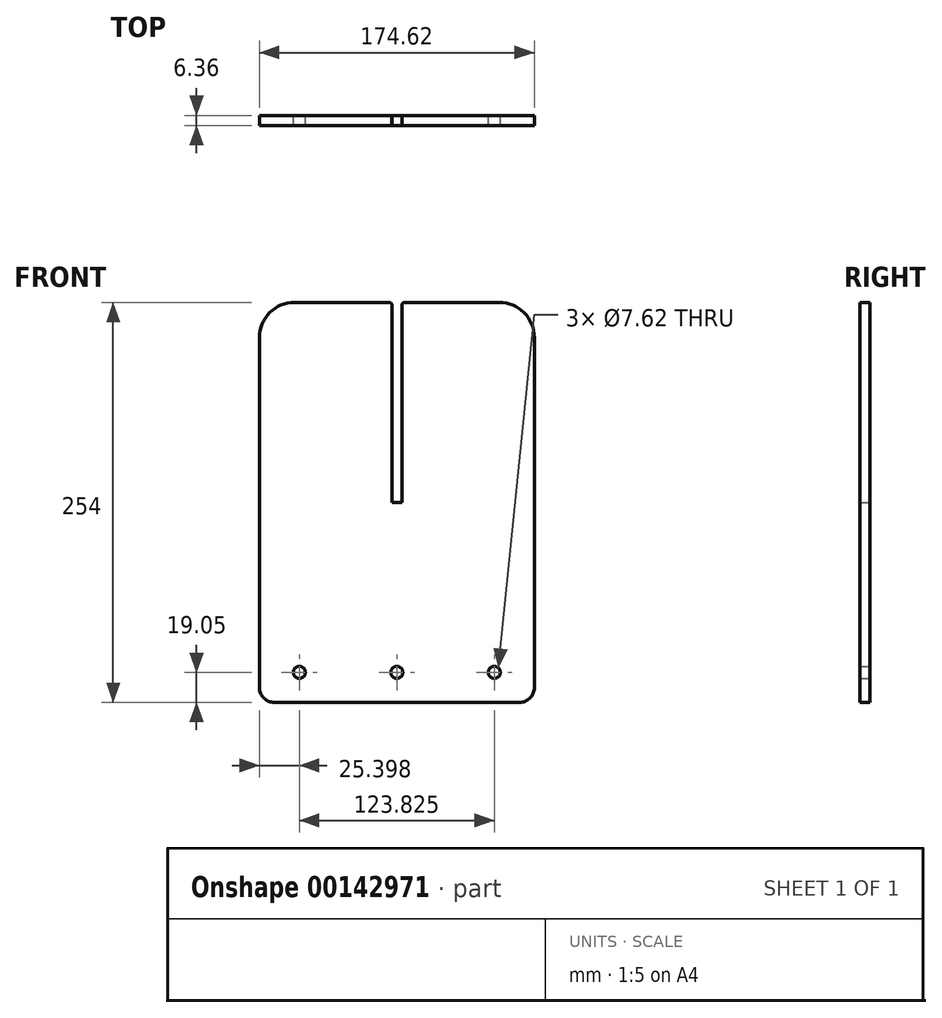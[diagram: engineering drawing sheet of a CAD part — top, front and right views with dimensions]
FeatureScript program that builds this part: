
annotation { "Feature Type Name" : "Feature", "Feature Type Description" : "" }
export const myFeature = defineFeature(function(context is Context, id is Id, definition is map)
    precondition{}
    {
        {
            var Q0;
            Q0=qCreatedBy(makeId("Front.planeOp"),FACE);
            var sketch = newSketch(context, id + "F0", { "sketchPlane" : qUnion([Q0])});
            skLineSegment(sketch, "E0.bottom", {"start": v(-65.09, 127) * mm, "end": v(-4.76, 127) * mm});
            skLineSegment(sketch, "E0.top", {"start": v(-77.79, -127) * mm, "end": v(77.79, -127) * mm});
            skLineSegment(sketch, "E0.left", {"start": v(-87.31, 104.78) * mm, "end": v(-87.31, -117.47) * mm});
            skLineSegment(sketch, "E0.right", {"start": v(87.31, 104.77) * mm, "end": v(87.31, -117.47) * mm});
            skPoint(sketch, "E0.middle", {"position": v(0, 0) * mm});
            skPoint(sketch, "E1.visualSharp", {"position": v(-87.31, 127) * mm});
            skArc(sketch, "E1.filletArc", {"start": v(-65.09, 127) * mm, "mid": v(-80.8, 120.5) * mm, "end": v(-87.31, 104.78) * mm});
            skPoint(sketch, "E2.visualSharp", {"position": v(87.31, 127) * mm});
            skArc(sketch, "E2.filletArc", {"start": v(87.31, 104.77) * mm, "mid": v(80.8, 120.5) * mm, "end": v(65.09, 127) * mm});
            skPoint(sketch, "E3.visualSharp", {"position": v(-87.31, -127) * mm});
            skArc(sketch, "E3.filletArc", {"start": v(-87.31, -117.47) * mm, "mid": v(-84.52, -124.21) * mm, "end": v(-77.79, -127) * mm});
            skPoint(sketch, "E4.visualSharp", {"position": v(87.31, -127) * mm});
            skArc(sketch, "E4.filletArc", {"start": v(77.79, -127) * mm, "mid": v(84.52, -124.21) * mm, "end": v(87.31, -117.47) * mm});
            skLineSegment(sketch, "E5", {"start": v(0, 0) * mm, "end": v(3.17, 0) * mm});
            skLineSegment(sketch, "E6", {"start": v(3.17, 0) * mm, "end": v(3.17, 125.41) * mm});
            skLineSegment(sketch, "E7.MirrorCS", {"start": v(-3.17, 0) * mm, "end": v(-3.17, 125.41) * mm});
            skLineSegment(sketch, "E8.MirrorCS", {"start": v(0, 0) * mm, "end": v(-3.17, 0) * mm});
            skLineSegment(sketch, "E9.trimOffspring", {"start": v(4.76, 127) * mm, "end": v(65.09, 127) * mm});
            skPoint(sketch, "E10.visualSharp", {"position": v(-3.17, 127) * mm});
            skArc(sketch, "E10.filletArc", {"start": v(-3.18, 125.41) * mm, "mid": v(-3.64, 126.54) * mm, "end": v(-4.76, 127) * mm});
            skPoint(sketch, "E11.visualSharp", {"position": v(3.17, 127) * mm});
            skArc(sketch, "E11.filletArc", {"start": v(4.76, 127) * mm, "mid": v(3.64, 126.54) * mm, "end": v(3.17, 125.41) * mm});
            skCircle(sketch, "E12", {"center": v(-61.91, -107.95) * mm, "radius": 3.81 * mm});
            skCircle(sketch, "E13", {"center": v(0, -107.95) * mm, "radius": 3.81 * mm});
            skCircle(sketch, "E14", {"center": v(61.91, -107.95) * mm, "radius": 3.81 * mm});
            skSolve(sketch);
        }
        {
            var Q0;
            Q0 = qSketchRegion(id + "F0", true);
            extrude(context, id + "F1", {"entities" : qUnion([Q0]), "endBound" : BoundingType.SYMMETRIC, "depth" : 6.35 * mm});
        }
    });
